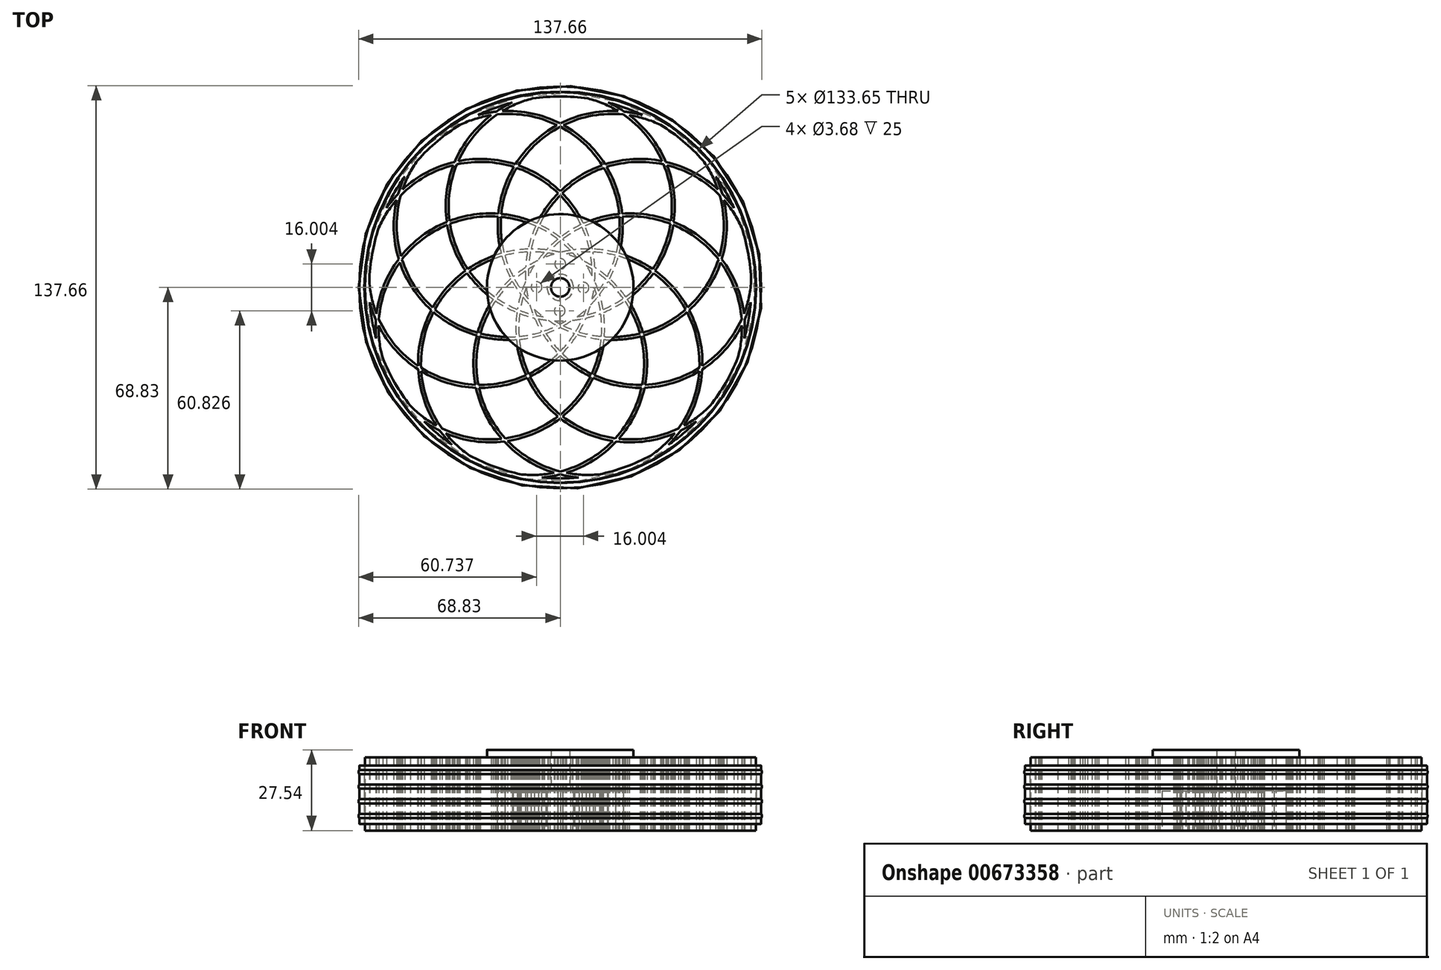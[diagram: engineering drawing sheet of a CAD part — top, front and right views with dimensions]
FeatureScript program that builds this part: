
annotation { "Feature Type Name" : "Feature", "Feature Type Description" : "" }
export const myFeature = defineFeature(function(context is Context, id is Id, definition is map)
    precondition{}
    {
        {
            var Q0;
            Q0=qCreatedBy(makeId("Top.planeOp"),FACE);
            var sketch = newSketch(context, id + "F0", { "sketchPlane" : qUnion([Q0])});
            skCircle(sketch, "E0", {"center": v(0, 0) * mm, "radius": 66.68 * mm});
            skCircle(sketch, "E1.0", {"center": v(0, 0) * mm, "radius": 65.18 * mm});
            skSolve(sketch);
        }
        {
            var Q0;
            Q0=qCreatedBy(makeId("Top.planeOp"),FACE);
            var sketch = newSketch(context, id + "F1", { "sketchPlane" : qUnion([Q0])});
            skPoint(sketch, "E2", {"position": v(0, -11.43) * mm});
            skCircle(sketch, "E3", {"center": v(0, 27.61) * mm, "radius": 39.06 * mm});
            skCircle(sketch, "E4.0", {"center": v(0, 27.61) * mm, "radius": 38.06 * mm});
            skSolve(sketch);
        }
        {
            var Q0;
            Q0=makeQuery(id+"F0.imprint","IMPRINT",FACE,{"disambiguationData":[TD([[makeQuery(id+"F0.imprint","IMPRINT",EDGE,{"derivedFrom":sQuery(id+"F0.wireOp",EDGE,"E0")}),1.0]])]});
            extrude(context, id + "F2", {"entities" : qUnion([Q0]), "depth" : 25 * mm, "offsetDistance" : 25 * mm, "symmetric" : true});
        }
        {
            var Q0;
            Q0=makeQuery(id+"F1.imprint","IMPRINT",FACE,{"disambiguationData":[TD([[makeQuery(id+"F1.imprint","IMPRINT",EDGE,{"derivedFrom":sQuery(id+"F1.wireOp",EDGE,"E3")}),1.0]])]});
            extrude(context, id + "F3", {"entities" : qUnion([Q0]), "depth" : 25 * mm, "offsetDistance" : 25 * mm, "symmetric" : true});
        }
        {
            var Q0;
            Q0=qCreatedBy(makeId("Right.planeOp"),FACE);
            var sketch = newSketch(context, id + "F4", { "sketchPlane" : qUnion([Q0])});
            skLineSegment(sketch, "E5", {"start": v(-11.46, 0) * mm, "end": v(-11.46, 66.16) * mm, "construction": true});
            skLineSegment(sketch, "E6", {"start": v(0, 72.05) * mm, "end": v(0, -72.65) * mm, "construction": true});
            skSolve(sketch);
        }
        {
            var Q0;
            Q0=makeQuery(id+"F3.opExtrude","SWEPT_BODY",BODY,{"disambiguationData":[OSD([sQuery(id+"F1.wireOp",EDGE,"E3"),sQuery(id+"F1.wireOp",EDGE,"E4.0")])]});
            var Q1;
            Q1=sQuery(id+"F4.wireOp",EDGE,"E6");
            circularPattern(context, id + "F5", {"entities" : qUnion([Q0]), "axis" : qUnion([Q1]), "angle" : 360 * degree, "instanceCount" : 9, "equalSpace" : true});
        }
        {
            var Q0;
            Q0=qCreatedBy(makeId("Top.planeOp"),FACE);
            var sketch = newSketch(context, id + "F6", { "sketchPlane" : qUnion([Q0])});
            skCircle(sketch, "E7.0", {"center": v(0, 8) * mm, "radius": 1.84 * mm});
            skCircle(sketch, "E8.0", {"center": v(-8.1, 0.09) * mm, "radius": 1.84 * mm});
            skCircle(sketch, "E9.0", {"center": v(7.91, -0.1) * mm, "radius": 1.84 * mm});
            skCircle(sketch, "E10.0", {"center": v(-0.18, -8) * mm, "radius": 1.84 * mm});
            skCircle(sketch, "E11", {"center": v(0, 0) * mm, "radius": 11.23 * mm});
            skCircle(sketch, "E12", {"center": v(0, 0) * mm, "radius": 4.5 * mm});
            skSolve(sketch);
        }
        {
            var Q0;
            Q0=qSketchRegion(id+"F6",true);
            extrude(context, id + "F7", {"entities" : qUnion([Q0]), "depth" : 25 * mm, "offsetDistance" : 25 * mm, "symmetric" : true});
        }
        {
            var Q0;
            Q0=makeQuery(id+"F2.opExtrude","SWEPT_BODY",BODY,{"disambiguationData":[OSD([sQuery(id+"F0.wireOp",EDGE,"E0"),sQuery(id+"F0.wireOp",EDGE,"E1.0")])]});
            var Q1;
            Q1=makeQuery(id+"F3.opExtrude","SWEPT_BODY",BODY,{"disambiguationData":[OSD([sQuery(id+"F1.wireOp",EDGE,"E3"),sQuery(id+"F1.wireOp",EDGE,"E4.0")])]});
            var Q2;
            Q2=makeQuery(id+"F5.opPattern","COPY",BODY,{"derivedFrom":makeQuery(id+"F3.opExtrude","SWEPT_BODY",BODY,{"disambiguationData":[OSD([sQuery(id+"F1.wireOp",EDGE,"E3"),sQuery(id+"F1.wireOp",EDGE,"E4.0")])]}),"instanceName":"1"});
            var Q3;
            Q3=makeQuery(id+"F5.opPattern","COPY",BODY,{"derivedFrom":makeQuery(id+"F3.opExtrude","SWEPT_BODY",BODY,{"disambiguationData":[OSD([sQuery(id+"F1.wireOp",EDGE,"E3"),sQuery(id+"F1.wireOp",EDGE,"E4.0")])]}),"instanceName":"4"});
            var Q4;
            Q4=makeQuery(id+"F5.opPattern","COPY",BODY,{"derivedFrom":makeQuery(id+"F3.opExtrude","SWEPT_BODY",BODY,{"disambiguationData":[OSD([sQuery(id+"F1.wireOp",EDGE,"E3"),sQuery(id+"F1.wireOp",EDGE,"E4.0")])]}),"instanceName":"5"});
            var Q5;
            Q5=makeQuery(id+"F5.opPattern","COPY",BODY,{"derivedFrom":makeQuery(id+"F3.opExtrude","SWEPT_BODY",BODY,{"disambiguationData":[OSD([sQuery(id+"F1.wireOp",EDGE,"E3"),sQuery(id+"F1.wireOp",EDGE,"E4.0")])]}),"instanceName":"7"});
            var Q6;
            Q6=makeQuery(id+"F5.opPattern","COPY",BODY,{"derivedFrom":makeQuery(id+"F3.opExtrude","SWEPT_BODY",BODY,{"disambiguationData":[OSD([sQuery(id+"F1.wireOp",EDGE,"E3"),sQuery(id+"F1.wireOp",EDGE,"E4.0")])]}),"instanceName":"3"});
            var Q7;
            Q7=makeQuery(id+"F5.opPattern","COPY",BODY,{"derivedFrom":makeQuery(id+"F3.opExtrude","SWEPT_BODY",BODY,{"disambiguationData":[OSD([sQuery(id+"F1.wireOp",EDGE,"E3"),sQuery(id+"F1.wireOp",EDGE,"E4.0")])]}),"instanceName":"6"});
            var Q8;
            Q8=makeQuery(id+"F5.opPattern","COPY",BODY,{"derivedFrom":makeQuery(id+"F3.opExtrude","SWEPT_BODY",BODY,{"disambiguationData":[OSD([sQuery(id+"F1.wireOp",EDGE,"E3"),sQuery(id+"F1.wireOp",EDGE,"E4.0")])]}),"instanceName":"8"});
            var Q9;
            Q9=makeQuery(id+"F5.opPattern","COPY",BODY,{"derivedFrom":makeQuery(id+"F3.opExtrude","SWEPT_BODY",BODY,{"disambiguationData":[OSD([sQuery(id+"F1.wireOp",EDGE,"E3"),sQuery(id+"F1.wireOp",EDGE,"E4.0")])]}),"instanceName":"2"});
            var Q10;
            Q10=makeQuery(id+"F7.opExtrude","SWEPT_BODY",BODY,{"disambiguationData":[OSD([sQuery(id+"F6.wireOp",EDGE,"E7.0"),sQuery(id+"F6.wireOp",EDGE,"E8.0"),sQuery(id+"F6.wireOp",EDGE,"E9.0"),sQuery(id+"F6.wireOp",EDGE,"E10.0"),sQuery(id+"F6.wireOp",EDGE,"E11"),sQuery(id+"F6.wireOp",EDGE,"E12")])]});
            booleanBodies(context, id + "F8", {"operationType" : BooleanOperationType.UNION, "tools" : qUnion([Q0, Q1, Q2, Q3, Q4, Q5, Q6, Q7, Q8, Q9, Q10])});
        }
        {
            var Q0;
            Q0=qCreatedBy(makeId("Front.planeOp"),FACE);
            var sketch = newSketch(context, id + "F9", { "sketchPlane" : qUnion([Q0])});
            skLineSegment(sketch, "E13.bottom", {"start": v(-67.08, -10.27) * mm, "end": v(-68.33, -10.27) * mm});
            skLineSegment(sketch, "E13.top", {"start": v(-67.08, 9.73) * mm, "end": v(-68.33, 9.73) * mm});
            skLineSegment(sketch, "E13.left", {"start": v(-66.83, -10.02) * mm, "end": v(-66.83, 9.48) * mm});
            skLineSegment(sketch, "E13.right", {"start": v(-68.58, -10.02) * mm, "end": v(-68.58, 9.48) * mm});
            skCircle(sketch, "E14", {"center": v(-67.7, 7.48) * mm, "radius": 1.13 * mm});
            skCircle(sketch, "E15.1.0.0", {"center": v(-67.7, 2.48) * mm, "radius": 1.13 * mm});
            skCircle(sketch, "E15.2.0.0", {"center": v(-67.7, -2.52) * mm, "radius": 1.13 * mm});
            skCircle(sketch, "E15.3.0.0", {"center": v(-67.7, -7.52) * mm, "radius": 1.13 * mm});
            skLineSegment(sketch, "E15.direction1", {"start": v(-67.7, 7.48) * mm, "end": v(-67.7, 2.48) * mm, "construction": true});
            skArc(sketch, "E16.filletArc", {"start": v(-68.33, 9.73) * mm, "mid": v(-68.5, 9.66) * mm, "end": v(-68.58, 9.48) * mm});
            skArc(sketch, "E17.filletArc", {"start": v(-66.83, 9.48) * mm, "mid": v(-66.9, 9.66) * mm, "end": v(-67.08, 9.73) * mm});
            skArc(sketch, "E18.filletArc", {"start": v(-67.08, -10.27) * mm, "mid": v(-66.9, -10.2) * mm, "end": v(-66.83, -10.02) * mm});
            skArc(sketch, "E19.filletArc", {"start": v(-68.58, -10.02) * mm, "mid": v(-68.5, -10.2) * mm, "end": v(-68.33, -10.27) * mm});
            skSolve(sketch);
        }
        {
            var Q0;
            Q0=qSketchRegion(id+"F9",true);
            var Q1;
            Q1=sQuery(id+"F0.wireOp",EDGE,"E0");
            revolve(context, id + "F10", {"entities" : qUnion([Q0]), "axis" : qUnion([Q1]), "revolveType" : RevolveType.FULL});
        }
        {
            var Q0;
            {var subQ0=makeQuery(id+"F3.opExtrude","CAP_FACE",FACE,{"disambiguationData":[OSD([sQuery(id+"F1.wireOp",EDGE,"E3"),sQuery(id+"F1.wireOp",EDGE,"E4.0")])],"isStart":false});Q0=makeQuery(id+"F8.opBoolean","MERGE",FACE,{"derivedFrom":[makeQuery(id+"F2.opExtrude","CAP_FACE",FACE,{"disambiguationData":[OSD([sQuery(id+"F0.wireOp",EDGE,"E0"),sQuery(id+"F0.wireOp",EDGE,"E1.0")])],"isStart":false}),subQ0,makeQuery(id+"F5.opPattern","COPY",FACE,{"derivedFrom":subQ0,"instanceName":"1"}),makeQuery(id+"F5.opPattern","COPY",FACE,{"derivedFrom":subQ0,"instanceName":"2"}),makeQuery(id+"F5.opPattern","COPY",FACE,{"derivedFrom":subQ0,"instanceName":"3"}),makeQuery(id+"F5.opPattern","COPY",FACE,{"derivedFrom":subQ0,"instanceName":"4"}),makeQuery(id+"F5.opPattern","COPY",FACE,{"derivedFrom":subQ0,"instanceName":"5"}),makeQuery(id+"F5.opPattern","COPY",FACE,{"derivedFrom":subQ0,"instanceName":"6"}),makeQuery(id+"F5.opPattern","COPY",FACE,{"derivedFrom":subQ0,"instanceName":"7"}),makeQuery(id+"F5.opPattern","COPY",FACE,{"derivedFrom":subQ0,"instanceName":"8"}),makeQuery(id+"F7.opExtrude","CAP_FACE",FACE,{"disambiguationData":[OSD([sQuery(id+"F6.wireOp",EDGE,"E7.0"),sQuery(id+"F6.wireOp",EDGE,"E8.0"),sQuery(id+"F6.wireOp",EDGE,"E9.0"),sQuery(id+"F6.wireOp",EDGE,"E10.0"),sQuery(id+"F6.wireOp",EDGE,"E11"),sQuery(id+"F6.wireOp",EDGE,"E12")])],"isStart":false})]});}
            var sketch = newSketch(context, id + "F11", { "sketchPlane" : qUnion([Q0])});
            skArc(sketch, "E20.0", {"start": v(-0.8, 16.44) * mm, "mid": v(-4.03, 18.65) * mm, "end": v(-7.47, 20.52) * mm});
            skArc(sketch, "E21.0", {"start": v(-7.47, 20.52) * mm, "mid": v(-8.9, 16.88) * mm, "end": v(-9.95, 13.11) * mm});
            skArc(sketch, "E22.0", {"start": v(-4.67, 12.82) * mm, "mid": v(-7.3, 13.05) * mm, "end": v(-9.95, 13.11) * mm});
            skArc(sketch, "E23.0", {"start": v(-0.8, 16.44) * mm, "mid": v(-2.8, 14.7) * mm, "end": v(-4.67, 12.82) * mm});
            skArc(sketch, "E24.0", {"start": v(4.67, 12.82) * mm, "mid": v(2.8, 14.7) * mm, "end": v(0.8, 16.44) * mm});
            skArc(sketch, "E25.0", {"start": v(7.47, 20.52) * mm, "mid": v(4.03, 18.65) * mm, "end": v(0.8, 16.44) * mm});
            skArc(sketch, "E26.0", {"start": v(9.95, 13.11) * mm, "mid": v(8.9, 16.88) * mm, "end": v(7.47, 20.52) * mm});
            skArc(sketch, "E27.0", {"start": v(9.95, 13.11) * mm, "mid": v(7.3, 13.05) * mm, "end": v(4.67, 12.82) * mm});
            skArc(sketch, "E28.0", {"start": v(21.5, -3.8) * mm, "mid": v(19.07, -0.73) * mm, "end": v(16.33, 2.06) * mm});
            skArc(sketch, "E29.0", {"start": v(13.44, -2.37) * mm, "mid": v(14.96, -0.2) * mm, "end": v(16.33, 2.06) * mm});
            skArc(sketch, "E30.0", {"start": v(14.64, -7.52) * mm, "mid": v(14.12, -4.92) * mm, "end": v(13.44, -2.37) * mm});
            skArc(sketch, "E31.0", {"start": v(14.64, -7.52) * mm, "mid": v(18.17, -5.83) * mm, "end": v(21.5, -3.8) * mm});
            skArc(sketch, "E32.0", {"start": v(8.77, -10.45) * mm, "mid": v(11.33, -9.77) * mm, "end": v(13.83, -8.92) * mm});
            skArc(sketch, "E33.0", {"start": v(6.38, -15.17) * mm, "mid": v(7.65, -12.85) * mm, "end": v(8.77, -10.45) * mm});
            skArc(sketch, "E34.0", {"start": v(6.38, -15.17) * mm, "mid": v(10.17, -16.15) * mm, "end": v(14.04, -16.73) * mm});
            skArc(sketch, "E35.0", {"start": v(14.04, -16.73) * mm, "mid": v(14.13, -12.82) * mm, "end": v(13.83, -8.92) * mm});
            skArc(sketch, "E36.0", {"start": v(0, -21.84) * mm, "mid": v(2.59, -18.9) * mm, "end": v(4.86, -15.72) * mm});
            skArc(sketch, "E37.0", {"start": v(0, -13.64) * mm, "mid": v(2.4, -14.76) * mm, "end": v(4.86, -15.72) * mm});
            skArc(sketch, "E38.0", {"start": v(-4.86, -15.72) * mm, "mid": v(-2.4, -14.76) * mm, "end": v(0, -13.64) * mm});
            skArc(sketch, "E39.0", {"start": v(-4.86, -15.72) * mm, "mid": v(-2.59, -18.9) * mm, "end": v(0, -21.84) * mm});
            skArc(sketch, "E40.0", {"start": v(-14.04, -16.73) * mm, "mid": v(-10.17, -16.15) * mm, "end": v(-6.38, -15.17) * mm});
            skArc(sketch, "E41.0", {"start": v(-13.83, -8.92) * mm, "mid": v(-11.33, -9.77) * mm, "end": v(-8.77, -10.45) * mm});
            skArc(sketch, "E42.0", {"start": v(-8.77, -10.45) * mm, "mid": v(-7.65, -12.85) * mm, "end": v(-6.38, -15.17) * mm});
            skArc(sketch, "E43.0", {"start": v(-13.83, -8.92) * mm, "mid": v(-14.13, -12.82) * mm, "end": v(-14.04, -16.73) * mm});
            skArc(sketch, "E44.0", {"start": v(-13.44, -2.37) * mm, "mid": v(-14.12, -4.92) * mm, "end": v(-14.64, -7.52) * mm});
            skArc(sketch, "E45.0", {"start": v(-21.5, -3.8) * mm, "mid": v(-18.17, -5.83) * mm, "end": v(-14.64, -7.52) * mm});
            skArc(sketch, "E46.0", {"start": v(-16.33, 2.06) * mm, "mid": v(-19.07, -0.73) * mm, "end": v(-21.5, -3.8) * mm});
            skArc(sketch, "E47.0", {"start": v(-16.33, 2.06) * mm, "mid": v(-14.96, -0.2) * mm, "end": v(-13.44, -2.37) * mm});
            skArc(sketch, "E48.0", {"start": v(-18.9, 10.92) * mm, "mid": v(-17.67, 7.2) * mm, "end": v(-16.05, 3.65) * mm});
            skArc(sketch, "E49.0", {"start": v(-11.18, 12.07) * mm, "mid": v(-15.08, 11.7) * mm, "end": v(-18.9, 10.92) * mm});
            skArc(sketch, "E50.0", {"start": v(-11.18, 12.07) * mm, "mid": v(-11.59, 9.46) * mm, "end": v(-11.81, 6.82) * mm});
            skArc(sketch, "E51.0", {"start": v(-11.81, 6.82) * mm, "mid": v(-13.99, 5.3) * mm, "end": v(-16.05, 3.65) * mm});
            skCircle(sketch, "E52.0", {"center": v(0, 0) * mm, "radius": 4.5 * mm});
            skPoint(sketch, "E53.0.end.orphan", {"position": v(10.16, 12.1) * mm});
            skPoint(sketch, "E53.0.start.orphan", {"position": v(10.77, 7.47) * mm});
            skArc(sketch, "E54.0", {"start": v(18.9, 10.92) * mm, "mid": v(15.08, 11.7) * mm, "end": v(11.18, 12.07) * mm});
            skArc(sketch, "E55.0", {"start": v(16.05, 3.65) * mm, "mid": v(17.67, 7.2) * mm, "end": v(18.9, 10.92) * mm});
            skPoint(sketch, "E56.0", {"position": v(13.99, 5.3) * mm});
            skArc(sketch, "E57.0", {"start": v(11.81, 6.82) * mm, "mid": v(11.59, 9.46) * mm, "end": v(11.18, 12.07) * mm});
            skArc(sketch, "E58.0", {"start": v(16.05, 3.65) * mm, "mid": v(13.99, 5.3) * mm, "end": v(11.81, 6.82) * mm});
            skCircle(sketch, "E59", {"center": v(0, 0) * mm, "radius": 25 * mm});
            skCircle(sketch, "E60", {"center": v(0, 0) * mm, "radius": 3.18 * mm});
            skSolve(sketch);
        }
        {
            var Q0;
            Q0=qSketchRegion(id+"F11",true);
            var Q1;
            Q1=makeQuery(id+"F11.imprint","IMPRINT",FACE,{"disambiguationData":[TD([[makeQuery(id+"F11.imprint","IMPRINT",EDGE,{"derivedFrom":sQuery(id+"F11.wireOp",EDGE,"E52.0")}),1.0]])]});
            var Q2;
            Q2=makeQuery(id+"F11.imprint","IMPRINT",FACE,{"disambiguationData":[TD([[makeQuery(id+"F11.imprint","IMPRINT",EDGE,{"derivedFrom":sQuery(id+"F11.wireOp",EDGE,"E44.0")}),-1.0]])]});
            var Q3;
            Q3=makeQuery(id+"F11.imprint","IMPRINT",FACE,{"disambiguationData":[TD([[makeQuery(id+"F11.imprint","IMPRINT",EDGE,{"derivedFrom":sQuery(id+"F11.wireOp",EDGE,"E48.0")}),1.0]])]});
            var Q4;
            Q4=makeQuery(id+"F11.imprint","IMPRINT",FACE,{"disambiguationData":[TD([[makeQuery(id+"F11.imprint","IMPRINT",EDGE,{"derivedFrom":sQuery(id+"F11.wireOp",EDGE,"E20.0")}),1.0]])]});
            var Q5;
            Q5=makeQuery(id+"F11.imprint","IMPRINT",FACE,{"disambiguationData":[TD([[makeQuery(id+"F11.imprint","IMPRINT",EDGE,{"derivedFrom":sQuery(id+"F11.wireOp",EDGE,"E24.0")}),-1.0]])]});
            var Q6;
            Q6=makeQuery(id+"F11.imprint","IMPRINT",FACE,{"disambiguationData":[TD([[makeQuery(id+"F11.imprint","IMPRINT",EDGE,{"derivedFrom":sQuery(id+"F11.wireOp",EDGE,"E54.0")}),1.0]])]});
            var Q7;
            Q7=makeQuery(id+"F11.imprint","IMPRINT",FACE,{"disambiguationData":[TD([[makeQuery(id+"F11.imprint","IMPRINT",EDGE,{"derivedFrom":sQuery(id+"F11.wireOp",EDGE,"E28.0")}),1.0]])]});
            var Q8;
            Q8=makeQuery(id+"F11.imprint","IMPRINT",FACE,{"disambiguationData":[TD([[makeQuery(id+"F11.imprint","IMPRINT",EDGE,{"derivedFrom":sQuery(id+"F11.wireOp",EDGE,"E32.0")}),-1.0]])]});
            var Q9;
            Q9=makeQuery(id+"F11.imprint","IMPRINT",FACE,{"disambiguationData":[TD([[makeQuery(id+"F11.imprint","IMPRINT",EDGE,{"derivedFrom":sQuery(id+"F11.wireOp",EDGE,"E36.0")}),1.0]])]});
            var Q10;
            Q10=makeQuery(id+"F11.imprint","IMPRINT",FACE,{"disambiguationData":[TD([[makeQuery(id+"F11.imprint","IMPRINT",EDGE,{"derivedFrom":sQuery(id+"F11.wireOp",EDGE,"E40.0")}),1.0]])]});
            extrude(context, id + "F12", {"entities" : qUnion([Q0, Q1, Q2, Q3, Q4, Q5, Q6, Q7, Q8, Q9, Q10]), "depth" : 2.54 * mm, "offsetDistance" : 25 * mm});
        }
        {
            var Q0;
            Q0=makeQuery(id+"F11.imprint","IMPRINT",FACE,{"disambiguationData":[TD([[makeQuery(id+"F11.imprint","IMPRINT",EDGE,{"derivedFrom":sQuery(id+"F11.wireOp",EDGE,"E40.0")}),1.0]])]});
            var Q1;
            Q1=makeQuery(id+"F11.imprint","IMPRINT",FACE,{"disambiguationData":[TD([[makeQuery(id+"F11.imprint","IMPRINT",EDGE,{"derivedFrom":sQuery(id+"F11.wireOp",EDGE,"E44.0")}),-1.0]])]});
            var Q2;
            Q2=makeQuery(id+"F11.imprint","IMPRINT",FACE,{"disambiguationData":[TD([[makeQuery(id+"F11.imprint","IMPRINT",EDGE,{"derivedFrom":sQuery(id+"F11.wireOp",EDGE,"E48.0")}),1.0]])]});
            var Q3;
            Q3=makeQuery(id+"F11.imprint","IMPRINT",FACE,{"disambiguationData":[TD([[makeQuery(id+"F11.imprint","IMPRINT",EDGE,{"derivedFrom":sQuery(id+"F11.wireOp",EDGE,"E20.0")}),1.0]])]});
            var Q4;
            Q4=makeQuery(id+"F11.imprint","IMPRINT",FACE,{"disambiguationData":[TD([[makeQuery(id+"F11.imprint","IMPRINT",EDGE,{"derivedFrom":sQuery(id+"F11.wireOp",EDGE,"E24.0")}),-1.0]])]});
            var Q5;
            Q5=makeQuery(id+"F11.imprint","IMPRINT",FACE,{"disambiguationData":[TD([[makeQuery(id+"F11.imprint","IMPRINT",EDGE,{"derivedFrom":sQuery(id+"F11.wireOp",EDGE,"E54.0")}),1.0]])]});
            var Q6;
            Q6=makeQuery(id+"F11.imprint","IMPRINT",FACE,{"disambiguationData":[TD([[makeQuery(id+"F11.imprint","IMPRINT",EDGE,{"derivedFrom":sQuery(id+"F11.wireOp",EDGE,"E28.0")}),1.0]])]});
            var Q7;
            Q7=makeQuery(id+"F11.imprint","IMPRINT",FACE,{"disambiguationData":[TD([[makeQuery(id+"F11.imprint","IMPRINT",EDGE,{"derivedFrom":sQuery(id+"F11.wireOp",EDGE,"E32.0")}),-1.0]])]});
            var Q8;
            Q8=makeQuery(id+"F11.imprint","IMPRINT",FACE,{"disambiguationData":[TD([[makeQuery(id+"F11.imprint","IMPRINT",EDGE,{"derivedFrom":sQuery(id+"F11.wireOp",EDGE,"E36.0")}),1.0]])]});
            var Q9;
            Q9=makeQuery(id+"F11.imprint","IMPRINT",FACE,{"disambiguationData":[TD([[makeQuery(id+"F11.imprint","IMPRINT",EDGE,{"derivedFrom":sQuery(id+"F11.wireOp",EDGE,"E52.0")}),1.0]])]});
            extrude(context, id + "F13", {"entities" : qUnion([Q0, Q1, Q2, Q3, Q4, Q5, Q6, Q7, Q8, Q9]), "operationType" : NewBodyOperationType.ADD, "oppositeDirection" : true, "depth" : 11.43 * mm, "offsetDistance" : 25 * mm});
        }
    });
